# Revit family: Towel_Bar-American_Standard-Studio_S-7105.224
name_source: partatom
category: Specialty Equipment
revit_build: Autodesk Revit 2018 (Build: 20170223_1515(x64)
units: mm (PartAtom-declared; Revit-internal decimal feet)

## family parameters
Cut with Voids When Loaded = No
Host = Face
OmniClass Number = 23.40.20.21.27
OmniClass Title = Towel Bars
Part Type = Normal
Room Calculation Point = No
Round Connector Dimension = Use Diameter
Shared = Yes

## types (1)
- 7105.224
    Assembly Code = C1030220
    Default Elevation = 48"
    Description = Studio S Double Towel Bar
    Finish = Metal-American Standard-002-Polished Chrome
    Height = 2"
    Installation Type = Wall Mounted
    Length = 24"
    Manufacturer = American Standard
    Material = Metal-American Standard-002-Polished Chrome
    Model = 7105.224
    Price = Prices may vary. Please consult Manufacturer Representative for most up-to-date price list.
    Product Documentation Link = https://www.americanstandard-us.com
    Product Page URL = https://www.americanstandard-us.com
    Specification = Studio S Double Towel Bar 24" shall feature metal construction. Rods shall be brass. Shall feature concealed mounting with no exposed set screws.
    URL = https://www.americanstandard-us.com
    Warranty Information = One Year General Product Warranty
    Width = 5 1/4"

## geometry (parser evidence)
native form markers: Sweep x3
no freeform markers — native parametric forms only
